# Revit family: TV-017-40_RFA
name_source: partatom
category: Aparatos sanitarios
units: mm (PartAtom-declared; Revit-internal decimal feet)

## family parameters
Activar corte en vistas = No
Compartido = Sí
Corte con vacíos al cargar = No
Cota de conector redondo = Usar diámetro
Mantener orientación de anotación = No
Número OmniClass = 23.45.00.00
Punto de cálculo de habitación = No
Se basa en plano de trabajo = No
Siempre vertical = Sí
Tipo de pieza = Normal
Título OmniClass = Sanitary, Laundry, and Cleaning Equipment

## types (1)
- TV-017-40
    Brass Chromed = Brass
    Comentarios de tipo = Lavatory Accesories
    Descripción = Large P-Trap With Cleanout Hole Without Drain
    Dune = Duna
    Elevación por defecto = 0"
    Fabricante = HELVEX
    Features = Cleaning Deposit; Hydraulic Seal
    Inlet Threads = Ø 1 ¼" - 14 NPT Pipe
    Instructive = http://helvex.com
    Matte Black = Ébano
    Modelo = TV-017-40
    Support Base Diameter = 3"
    Titanium = Titanio
    Total Height = 5"
    Total Length = 16"
    URL = http://helvex.com

## geometry (parser evidence)
native form markers: Sweep x3
no freeform markers — native parametric forms only
